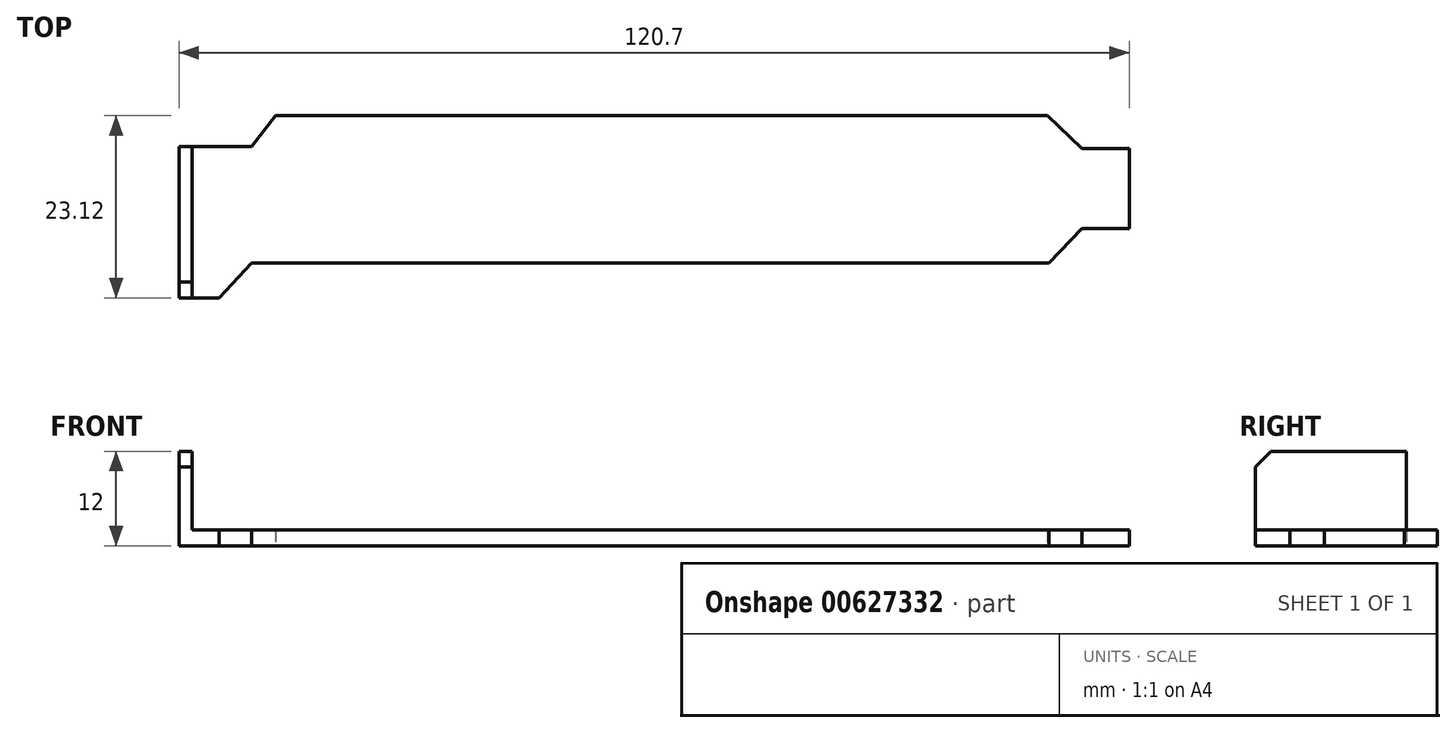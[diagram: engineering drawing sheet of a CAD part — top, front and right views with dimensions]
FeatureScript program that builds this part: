
annotation { "Feature Type Name" : "Feature", "Feature Type Description" : "" }
export const myFeature = defineFeature(function(context is Context, id is Id, definition is map)
    precondition{}
    {
        {
            var Q0;
            Q0=qCreatedBy(makeId("Top.planeOp"),FACE);
            var sketch = newSketch(context, id + "F0", { "sketchPlane" : qUnion([Q0])});
            skLineSegment(sketch, "E0", {"start": v(-43.36, 9.13) * mm, "end": v(54.69, 9.13) * mm});
            skLineSegment(sketch, "E1", {"start": v(54.69, 9.13) * mm, "end": v(59.08, 4.97) * mm});
            skLineSegment(sketch, "E2", {"start": v(59.08, 4.97) * mm, "end": v(65.1, 4.97) * mm});
            skLineSegment(sketch, "E3", {"start": v(65.1, 4.97) * mm, "end": v(65.1, -5.2) * mm});
            skLineSegment(sketch, "E4", {"start": v(65.1, -5.2) * mm, "end": v(59.08, -5.2) * mm});
            skLineSegment(sketch, "E5", {"start": v(59.08, -5.2) * mm, "end": v(54.92, -9.6) * mm});
            skLineSegment(sketch, "E6", {"start": v(54.92, -9.6) * mm, "end": v(-46.36, -9.6) * mm});
            skLineSegment(sketch, "E7", {"start": v(-46.36, -9.6) * mm, "end": v(-50.53, -14) * mm});
            skLineSegment(sketch, "E8", {"start": v(-50.53, -14) * mm, "end": v(-55.61, -14) * mm});
            skLineSegment(sketch, "E9", {"start": v(-55.61, -14) * mm, "end": v(-55.61, 5.2) * mm});
            skLineSegment(sketch, "E10", {"start": v(-55.61, 5.2) * mm, "end": v(-46.36, 5.2) * mm});
            skLineSegment(sketch, "E11", {"start": v(-46.36, 5.2) * mm, "end": v(-43.36, 9.13) * mm});
            skLineSegment(sketch, "E12", {"start": v(-53.93, 5.2) * mm, "end": v(-53.93, -14) * mm});
            skSolve(sketch);
        }
        {
            var Q0;
            {var subQ0=sQuery(id+"F0.wireOp",EDGE,"E9");Q0=makeQuery(id+"F0.imprint","IMPRINT",FACE,{"disambiguationData":[TD([[makeQuery(id+"F0.imprint","IMPRINT",EDGE,{"derivedFrom":subQ0}),-1.0]])]});}
            extrude(context, id + "F1", {"entities" : qUnion([Q0]), "depth" : 12 * mm, "offsetDistance" : 25 * mm});
        }
        {
            var Q0;
            Q0 = qSketchRegion(id + "F0", true);
            extrude(context, id + "F2", {"entities" : qUnion([Q0]), "operationType" : NewBodyOperationType.ADD, "depth" : 2 * mm, "offsetDistance" : 25 * mm});
        }
        {
            var Q0;
            Q0=makeQuery(id+"F1.opExtrude","CAP_EDGE",EDGE,{"disambiguationData":[OSD([sQuery(id+"F0.wireOp",EDGE,"E8")])],"isStart":false});
            chamfer(context, id + "F3", {"entities" : qUnion([Q0]), "width" : 2 * mm, "tangentPropagation" : true});
        }
    });
